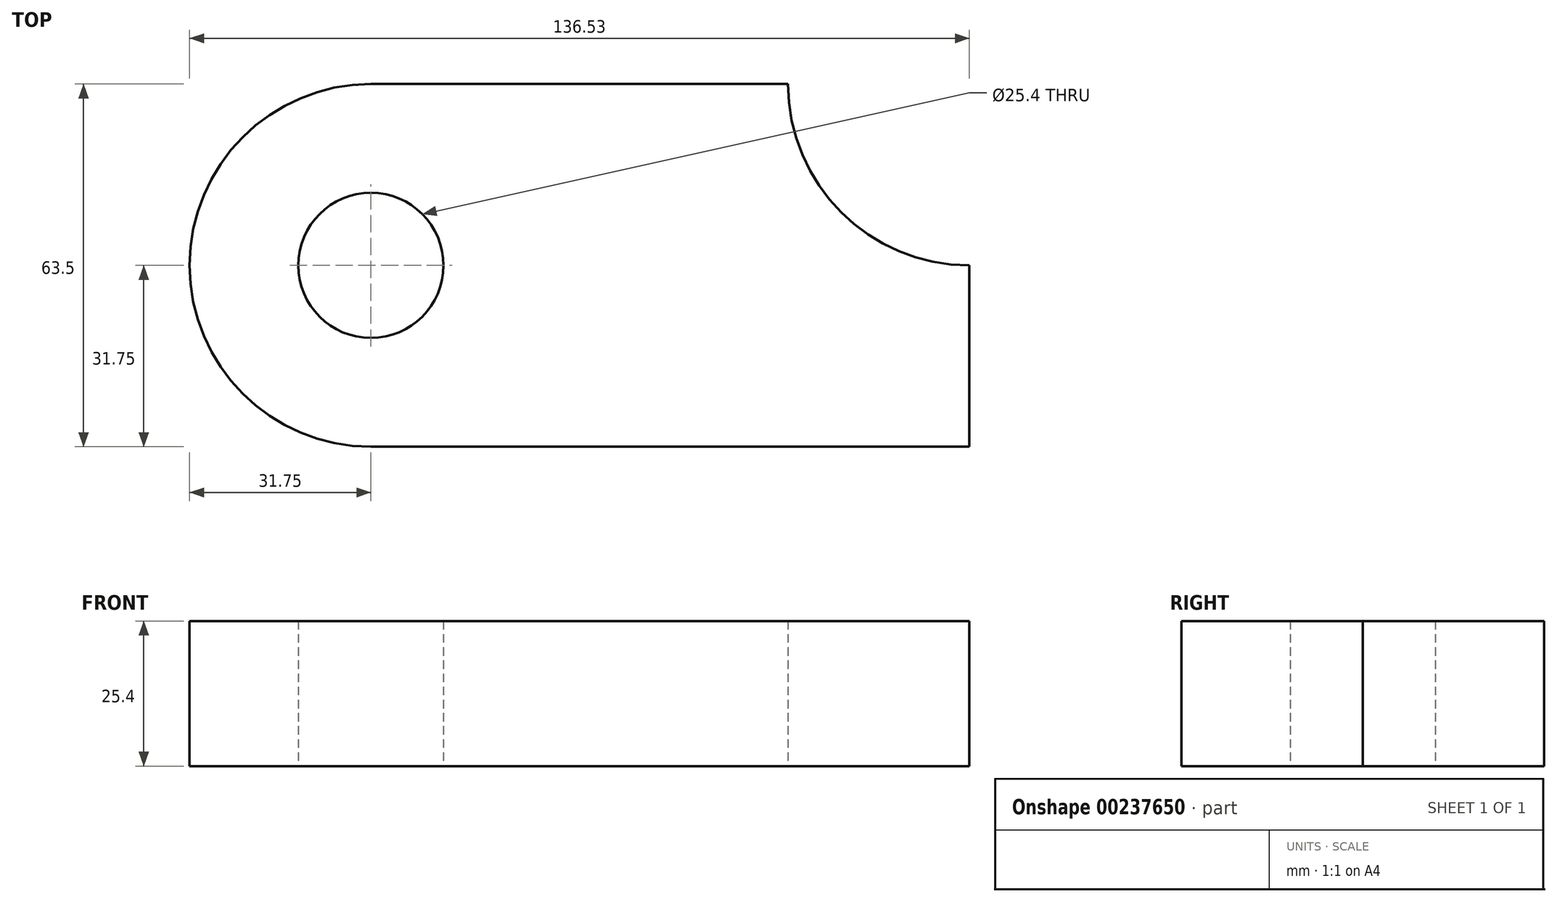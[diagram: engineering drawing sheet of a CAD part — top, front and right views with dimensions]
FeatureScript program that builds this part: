
annotation { "Feature Type Name" : "Feature", "Feature Type Description" : "" }
export const myFeature = defineFeature(function(context is Context, id is Id, definition is map)
    precondition{}
    {
        {
            var Q0;
            Q0=qCreatedBy(makeId("Top.planeOp"),FACE);
            var sketch = newSketch(context, id + "F0", { "sketchPlane" : qUnion([Q0])});
            skLineSegment(sketch, "E0.bottom", {"start": v(31.75, 0) * mm, "end": v(136.53, 0) * mm});
            skLineSegment(sketch, "E0.top", {"start": v(31.75, 63.5) * mm, "end": v(104.78, 63.5) * mm});
            skLineSegment(sketch, "E0.right", {"start": v(136.53, 0) * mm, "end": v(136.53, 31.75) * mm});
            skLineSegment(sketch, "E1", {"start": v(104.78, 63.5) * mm, "end": v(31.75, 63.5) * mm});
            skArc(sketch, "E2", {"start": v(31.75, 63.5) * mm, "mid": v(0, 31.75) * mm, "end": v(31.75, 0) * mm});
            skCircle(sketch, "E3", {"center": v(31.75, 31.75) * mm, "radius": 12.7 * mm});
            skArc(sketch, "E4", {"start": v(104.78, 63.5) * mm, "mid": v(114.07, 41.05) * mm, "end": v(136.53, 31.75) * mm});
            skPoint(sketch, "E5.end.orphan", {"position": v(31.75, 0) * mm});
            skSolve(sketch);
        }
        {
            var Q0;
            Q0=makeQuery(id+"F0.imprint","IMPRINT",FACE,{"disambiguationData":[TD([[makeQuery(id+"F0.imprint","IMPRINT",EDGE,{"derivedFrom":sQuery(id+"F0.wireOp",EDGE,"E0.bottom")}),1.0]])]});
            extrude(context, id + "F1", {"entities" : qUnion([Q0]), "depth" : 25.4 * mm});
        }
    });
